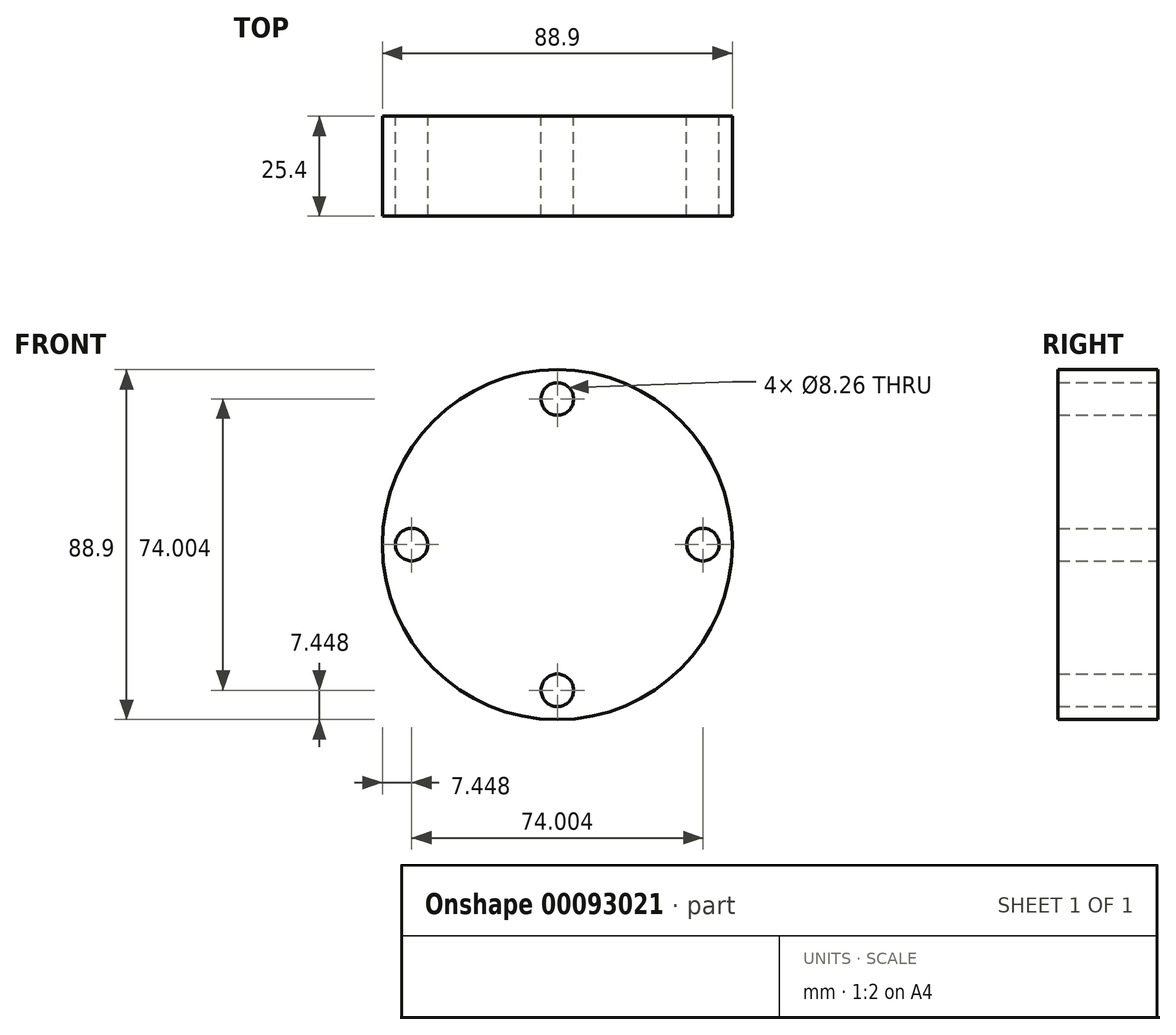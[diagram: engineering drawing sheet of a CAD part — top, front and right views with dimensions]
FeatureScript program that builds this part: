
annotation { "Feature Type Name" : "Feature", "Feature Type Description" : "" }
export const myFeature = defineFeature(function(context is Context, id is Id, definition is map)
    precondition{}
    {
        {
            var Q0;
            Q0=qCreatedBy(makeId("Front.planeOp"),FACE);
            var sketch = newSketch(context, id + "F0", { "sketchPlane" : qUnion([Q0])});
            skCircle(sketch, "E0", {"center": v(0, 0) * mm, "radius": 44.45 * mm});
            skCircle(sketch, "E1", {"center": v(0, 37) * mm, "radius": 4.13 * mm});
            skCircle(sketch, "E2.1.0", {"center": v(37, 0) * mm, "radius": 4.13 * mm});
            skCircle(sketch, "E2.2.0", {"center": v(0, -37) * mm, "radius": 4.13 * mm});
            skCircle(sketch, "E2.3.0", {"center": v(-37, 0) * mm, "radius": 4.13 * mm});
            skLineSegment(sketch, "E2.anchor1", {"start": v(0, 0) * mm, "end": v(0, 37) * mm, "construction": true});
            skLineSegment(sketch, "E2.anchor2", {"start": v(0, 0) * mm, "end": v(-37, 0) * mm, "construction": true});
            skSolve(sketch);
        }
        {
            var Q0;
            Q0 = qSketchRegion(id + "F0", true);
            extrude(context, id + "F1", {"entities" : qUnion([Q0]), "endBound" : BoundingType.SYMMETRIC, "depth" : 25.4 * mm});
        }
    });
